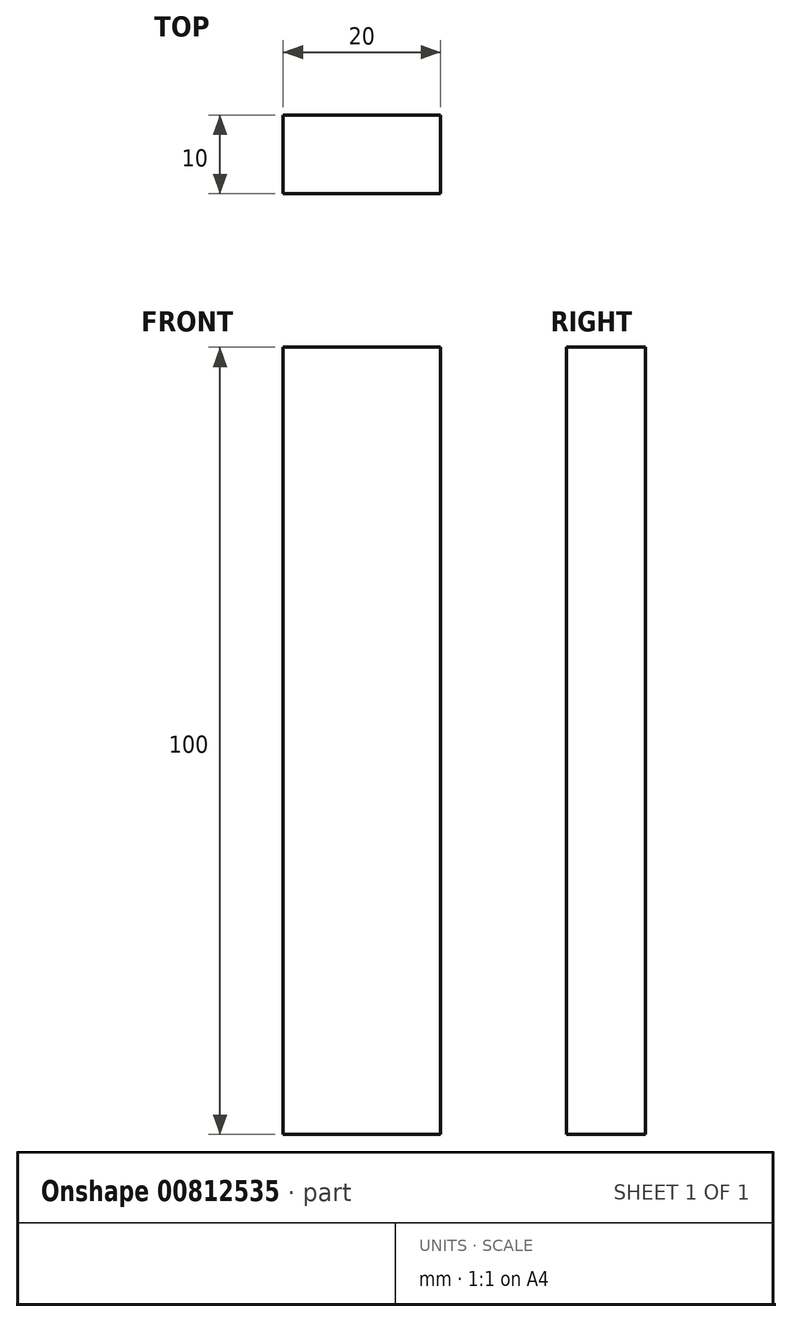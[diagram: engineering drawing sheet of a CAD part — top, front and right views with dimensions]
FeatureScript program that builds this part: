
annotation { "Feature Type Name" : "Feature", "Feature Type Description" : "" }
export const myFeature = defineFeature(function(context is Context, id is Id, definition is map)
    precondition{}
    {
        {
            var Q0;
            Q0=qCreatedBy(makeId("Top.planeOp"),FACE);
            var sketch = newSketch(context, id + "F0", { "sketchPlane" : qUnion([Q0])});
            skLineSegment(sketch, "E0.bottom", {"start": v(-10, 5) * mm, "end": v(10, 5) * mm});
            skLineSegment(sketch, "E0.top", {"start": v(-10, -5) * mm, "end": v(10, -5) * mm});
            skLineSegment(sketch, "E0.left", {"start": v(-10, 5) * mm, "end": v(-10, -5) * mm});
            skLineSegment(sketch, "E0.right", {"start": v(10, 5) * mm, "end": v(10, -5) * mm});
            skSolve(sketch);
        }
        {
            var Q0;
            Q0=makeQuery(id+"F0.imprint","IMPRINT",FACE,{"disambiguationData":[TD([[makeQuery(id+"F0.imprint","IMPRINT",EDGE,{"derivedFrom":sQuery(id+"F0.wireOp",EDGE,"E0.bottom")}),-1.0]])]});
            extrude(context, id + "F1", {"entities" : qUnion([Q0]), "depth" : 100 * mm, "offsetDistance" : 25 * mm});
        }
    });
